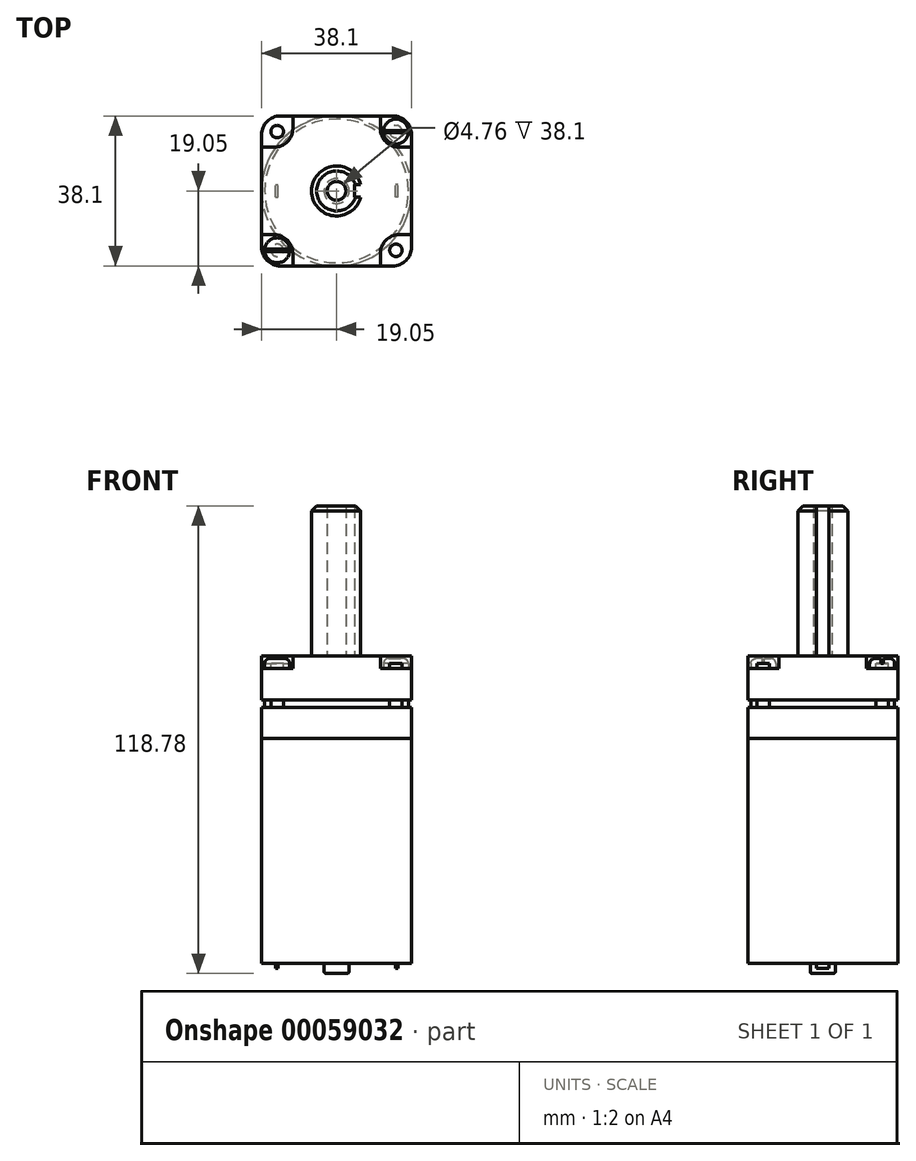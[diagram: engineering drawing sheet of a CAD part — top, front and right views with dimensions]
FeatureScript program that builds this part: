
annotation { "Feature Type Name" : "Feature", "Feature Type Description" : "" }
export const myFeature = defineFeature(function(context is Context, id is Id, definition is map)
    precondition{}
    {
        {
            var Q0;
            Q0=qCreatedBy(makeId("Top.planeOp"),FACE);
            var sketch = newSketch(context, id + "F0", { "sketchPlane" : qUnion([Q0])});
            skLineSegment(sketch, "E0.rect.bottom", {"start": v(-19.05, 19.05) * mm, "end": v(19.05, 19.05) * mm});
            skLineSegment(sketch, "E0.rect.top", {"start": v(-19.05, -19.05) * mm, "end": v(19.05, -19.05) * mm});
            skLineSegment(sketch, "E0.rect.left", {"start": v(-19.05, 19.05) * mm, "end": v(-19.05, -19.05) * mm});
            skLineSegment(sketch, "E0.rect.right", {"start": v(19.05, 19.05) * mm, "end": v(19.05, -19.05) * mm});
            skPoint(sketch, "E0.rect.middle", {"position": v(0, 0) * mm});
            skSolve(sketch);
        }
        {
            var Q0;
            Q0=qSketchRegion(id+"F0",true);
            extrude(context, id + "F1", {"entities" : qUnion([Q0]), "depth" : 7.94 * mm});
        }
        {
            var Q0;
            Q0=makeQuery(id+"F1.opExtrude","CAP_FACE",FACE,{"disambiguationData":[OSD([sQuery(id+"F0.wireOp",EDGE,"E0.rect.bottom"),sQuery(id+"F0.wireOp",EDGE,"E0.rect.top"),sQuery(id+"F0.wireOp",EDGE,"E0.rect.left"),sQuery(id+"F0.wireOp",EDGE,"E0.rect.right")])],"isStart":false});
            var sketch = newSketch(context, id + "F2", { "sketchPlane" : qUnion([Q0])});
            skCircle(sketch, "E1", {"center": v(0, 0) * mm, "radius": 18.26 * mm});
            skSolve(sketch);
        }
        {
            var Q0;
            Q0=makeQuery(id+"F2.imprint","IMPRINT",FACE,{"disambiguationData":[TD([[makeQuery(id+"F2.imprint","IMPRINT",EDGE,{"derivedFrom":sQuery(id+"F2.wireOp",EDGE,"E1")}),1.0]])]});
            extrude(context, id + "F3", {"entities" : qUnion([Q0]), "operationType" : NewBodyOperationType.ADD, "depth" : (1 + (15 / 16)) * mm});
        }
        {
            var Q0;
            Q0=makeQuery(id+"F1.opExtrude","CAP_FACE",FACE,{"disambiguationData":[OSD([sQuery(id+"F0.wireOp",EDGE,"E0.rect.bottom"),sQuery(id+"F0.wireOp",EDGE,"E0.rect.top"),sQuery(id+"F0.wireOp",EDGE,"E0.rect.left"),sQuery(id+"F0.wireOp",EDGE,"E0.rect.right")])],"isStart":true});
            var sketch = newSketch(context, id + "F4", { "sketchPlane" : qUnion([Q0])});
            skCircle(sketch, "E2", {"center": v(0, 0) * mm, "radius": 19.05 * mm});
            skSolve(sketch);
        }
        {
            var Q0;
            {var subQ0=sQuery(id+"F4.wireOp",EDGE,"E2");var subQ1=makeQuery(id+"F4.imprint","INTERSECT",VERTEX,{"derivedFrom":[makeQuery(id+"F1.opExtrude","CAP_EDGE",EDGE,{"disambiguationData":[OSD([sQuery(id+"F0.wireOp",EDGE,"E0.rect.top")])],"isStart":true}),subQ0]});Q0=makeQuery(id+"F4.imprint","IMPRINT",FACE,{"disambiguationData":[TD([[makeQuery(id+"F4.imprint","IMPRINT",EDGE,{"disambiguationData":[TD([[subQ1,1.0]])],"derivedFrom":subQ0}),1.0]])]});}
            extrude(context, id + "F5", {"entities" : qUnion([Q0]), "operationType" : NewBodyOperationType.ADD, "depth" : 57.15 * mm});
        }
        {
            var Q0;
            Q0=makeQuery(id+"F3.opExtrude","CAP_FACE",FACE,{"disambiguationData":[OSD([sQuery(id+"F2.wireOp",EDGE,"E1")])],"isStart":false});
            var sketch = newSketch(context, id + "F6", { "sketchPlane" : qUnion([Q0])});
            skLineSegment(sketch, "E3.rect.bottom", {"start": v(19.05, -19.05) * mm, "end": v(-19.05, -19.05) * mm});
            skLineSegment(sketch, "E3.rect.top", {"start": v(19.05, 19.05) * mm, "end": v(-19.05, 19.05) * mm});
            skLineSegment(sketch, "E3.rect.left", {"start": v(19.05, -19.05) * mm, "end": v(19.05, 19.05) * mm});
            skLineSegment(sketch, "E3.rect.right", {"start": v(-19.05, -19.05) * mm, "end": v(-19.05, 19.05) * mm});
            skPoint(sketch, "E3.rect.middle", {"position": v(0, 0) * mm});
            skSolve(sketch);
        }
        {
            var Q0;
            Q0=qSketchRegion(id+"F6",true);
            extrude(context, id + "F7", {"entities" : qUnion([Q0]), "operationType" : NewBodyOperationType.ADD, "depth" : 11.1 * mm});
        }
        {
            var Q0;
            Q0=makeQuery(id+"F7.opExtrude","CAP_FACE",FACE,{"disambiguationData":[OSD([sQuery(id+"F6.wireOp",EDGE,"E3.rect.bottom"),sQuery(id+"F6.wireOp",EDGE,"E3.rect.top"),sQuery(id+"F6.wireOp",EDGE,"E3.rect.left"),sQuery(id+"F6.wireOp",EDGE,"E3.rect.right")])],"isStart":false});
            var sketch = newSketch(context, id + "F8", { "sketchPlane" : qUnion([Q0])});
            skLineSegment(sketch, "E4", {"start": v(-19.05, -11.11) * mm, "end": v(-11.11, -11.11) * mm});
            skLineSegment(sketch, "E5", {"start": v(-11.11, -11.11) * mm, "end": v(-11.11, -19.05) * mm});
            skLineSegment(sketch, "E6", {"start": v(-11.11, -19.05) * mm, "end": v(-19.05, -19.05) * mm});
            skLineSegment(sketch, "E7", {"start": v(-19.05, -19.05) * mm, "end": v(-19.05, -11.11) * mm});
            skLineSegment(sketch, "E8.MirrorCS", {"start": v(11.11, -11.11) * mm, "end": v(11.11, -19.05) * mm});
            skLineSegment(sketch, "E9.MirrorCS", {"start": v(19.05, -11.11) * mm, "end": v(11.11, -11.11) * mm});
            skLineSegment(sketch, "E10.MirrorCS", {"start": v(19.05, -19.05) * mm, "end": v(19.05, -11.11) * mm});
            skLineSegment(sketch, "E11.MirrorCS", {"start": v(11.11, -19.05) * mm, "end": v(19.05, -19.05) * mm});
            skLineSegment(sketch, "E12.MirrorCS", {"start": v(19.05, 11.11) * mm, "end": v(11.11, 11.11) * mm});
            skLineSegment(sketch, "E13.MirrorCS", {"start": v(11.11, 11.11) * mm, "end": v(11.11, 19.05) * mm});
            skLineSegment(sketch, "E14.MirrorCS", {"start": v(11.11, 19.05) * mm, "end": v(19.05, 19.05) * mm});
            skLineSegment(sketch, "E15.MirrorCS", {"start": v(19.05, 19.05) * mm, "end": v(19.05, 11.11) * mm});
            skLineSegment(sketch, "E16.MirrorCS", {"start": v(-19.05, 11.11) * mm, "end": v(-11.11, 11.11) * mm});
            skLineSegment(sketch, "E17.MirrorCS", {"start": v(-11.11, 11.11) * mm, "end": v(-11.11, 19.05) * mm});
            skLineSegment(sketch, "E18.MirrorCS", {"start": v(-11.11, 19.05) * mm, "end": v(-19.05, 19.05) * mm});
            skLineSegment(sketch, "E19.MirrorCS", {"start": v(-19.05, 19.05) * mm, "end": v(-19.05, 11.11) * mm});
            skSolve(sketch);
        }
        {
            var Q0;
            Q0=makeQuery(id+"F8.imprint","IMPRINT",FACE,{"disambiguationData":[TD([[makeQuery(id+"F8.imprint","IMPRINT",EDGE,{"derivedFrom":sQuery(id+"F8.wireOp",EDGE,"E16.MirrorCS")}),1.0]])]});
            var Q1;
            Q1=makeQuery(id+"F8.imprint","IMPRINT",FACE,{"disambiguationData":[TD([[makeQuery(id+"F8.imprint","IMPRINT",EDGE,{"derivedFrom":sQuery(id+"F8.wireOp",EDGE,"E12.MirrorCS")}),-1.0]])]});
            var Q2;
            Q2=makeQuery(id+"F8.imprint","IMPRINT",FACE,{"disambiguationData":[TD([[makeQuery(id+"F8.imprint","IMPRINT",EDGE,{"derivedFrom":sQuery(id+"F8.wireOp",EDGE,"E8.MirrorCS")}),1.0]])]});
            var Q3;
            Q3=makeQuery(id+"F8.imprint","IMPRINT",FACE,{"disambiguationData":[TD([[makeQuery(id+"F8.imprint","IMPRINT",EDGE,{"derivedFrom":sQuery(id+"F8.wireOp",EDGE,"E4")}),-1.0]])]});
            extrude(context, id + "F9", {"entities" : qUnion([Q0, Q1, Q2, Q3]), "operationType" : NewBodyOperationType.REMOVE, "oppositeDirection" : true, "depth" : 3.17 * mm});
        }
        {
            var Q0;
            Q0=makeQuery(id+"F7.opExtrude","SWEPT_EDGE",EDGE,{"disambiguationData":[OSD([sQuery(id+"F6.wireOp",EDGE,"E3.rect.bottom"),sQuery(id+"F6.wireOp",EDGE,"E3.rect.right")])]});
            var Q1;
            Q1=makeQuery(id+"F7.opExtrude","SWEPT_EDGE",EDGE,{"disambiguationData":[OSD([sQuery(id+"F6.wireOp",EDGE,"E3.rect.bottom"),sQuery(id+"F6.wireOp",EDGE,"E3.rect.left")])]});
            var Q2;
            Q2=makeQuery(id+"F1.opExtrude","SWEPT_EDGE",EDGE,{"disambiguationData":[OSD([sQuery(id+"F0.wireOp",EDGE,"E0.rect.top"),sQuery(id+"F0.wireOp",EDGE,"E0.rect.right")])]});
            var Q3;
            Q3=makeQuery(id+"F1.opExtrude","SWEPT_EDGE",EDGE,{"disambiguationData":[OSD([sQuery(id+"F0.wireOp",EDGE,"E0.rect.top"),sQuery(id+"F0.wireOp",EDGE,"E0.rect.left")])]});
            var Q4;
            Q4=makeQuery(id+"F1.opExtrude","SWEPT_EDGE",EDGE,{"disambiguationData":[OSD([sQuery(id+"F0.wireOp",EDGE,"E0.rect.bottom"),sQuery(id+"F0.wireOp",EDGE,"E0.rect.right")])]});
            var Q5;
            Q5=makeQuery(id+"F7.opExtrude","SWEPT_EDGE",EDGE,{"disambiguationData":[OSD([sQuery(id+"F6.wireOp",EDGE,"E3.rect.top"),sQuery(id+"F6.wireOp",EDGE,"E3.rect.left")])]});
            var Q6;
            Q6=makeQuery(id+"F1.opExtrude","SWEPT_EDGE",EDGE,{"disambiguationData":[OSD([sQuery(id+"F0.wireOp",EDGE,"E0.rect.bottom"),sQuery(id+"F0.wireOp",EDGE,"E0.rect.left")])]});
            var Q7;
            Q7=makeQuery(id+"F7.opExtrude","SWEPT_EDGE",EDGE,{"disambiguationData":[OSD([sQuery(id+"F6.wireOp",EDGE,"E3.rect.top"),sQuery(id+"F6.wireOp",EDGE,"E3.rect.right")])]});
            fillet(context, id + "F10", {"entities" : qUnion([Q0, Q1, Q2, Q3, Q4, Q5, Q6, Q7]), "radius" : 4.76 * mm, "tangentPropagation" : true, "allowEdgeOverflow" : false});
        }
        {
            var Q0;
            Q0=makeQuery(id+"F9.boolean.opBoolean","COPY",EDGE,{"derivedFrom":makeQuery(id+"F9.opExtrude","SWEPT_EDGE",EDGE,{"disambiguationData":[OSD([sQuery(id+"F8.wireOp",EDGE,"E8.MirrorCS"),sQuery(id+"F8.wireOp",EDGE,"E9.MirrorCS")])]})});
            var Q1;
            Q1=makeQuery(id+"F9.boolean.opBoolean","COPY",EDGE,{"derivedFrom":makeQuery(id+"F9.opExtrude","SWEPT_EDGE",EDGE,{"disambiguationData":[OSD([sQuery(id+"F8.wireOp",EDGE,"E4"),sQuery(id+"F8.wireOp",EDGE,"E5")])]})});
            var Q2;
            Q2=makeQuery(id+"F9.boolean.opBoolean","COPY",EDGE,{"derivedFrom":makeQuery(id+"F9.opExtrude","SWEPT_EDGE",EDGE,{"disambiguationData":[OSD([sQuery(id+"F8.wireOp",EDGE,"E12.MirrorCS"),sQuery(id+"F8.wireOp",EDGE,"E13.MirrorCS")])]})});
            var Q3;
            Q3=makeQuery(id+"F9.boolean.opBoolean","COPY",EDGE,{"derivedFrom":makeQuery(id+"F9.opExtrude","SWEPT_EDGE",EDGE,{"disambiguationData":[OSD([sQuery(id+"F8.wireOp",EDGE,"E16.MirrorCS"),sQuery(id+"F8.wireOp",EDGE,"E17.MirrorCS")])]})});
            fillet(context, id + "F11", {"entities" : qUnion([Q0, Q1, Q2, Q3]), "radius" : 4.76 * mm, "tangentPropagation" : true, "allowEdgeOverflow" : false});
        }
        {
            var Q0;
            Q0=makeQuery(id+"F9.boolean.opBoolean","COPY",FACE,{"derivedFrom":makeQuery(id+"F9.opExtrude","CAP_FACE",FACE,{"disambiguationData":[OSD([sQuery(id+"F8.wireOp",EDGE,"E12.MirrorCS"),sQuery(id+"F8.wireOp",EDGE,"E13.MirrorCS"),sQuery(id+"F8.wireOp",EDGE,"E14.MirrorCS"),sQuery(id+"F8.wireOp",EDGE,"E15.MirrorCS")])],"isStart":false})});
            var sketch = newSketch(context, id + "F12", { "sketchPlane" : qUnion([Q0])});
            skCircle(sketch, "E20", {"center": v(15.08, 15.08) * mm, "radius": 3.18 * mm});
            skCircle(sketch, "E21.MirrorC", {"center": v(-15.08, 15.08) * mm, "radius": 3.18 * mm});
            skCircle(sketch, "E22.MirrorC", {"center": v(-15.08, -15.08) * mm, "radius": 3.18 * mm});
            skCircle(sketch, "E23.MirrorC", {"center": v(15.08, -15.08) * mm, "radius": 3.18 * mm});
            skSolve(sketch);
        }
        {
            var Q0;
            Q0=makeQuery(id+"F12.imprint","IMPRINT",FACE,{"disambiguationData":[TD([[makeQuery(id+"F12.imprint","IMPRINT",EDGE,{"derivedFrom":sQuery(id+"F12.wireOp",EDGE,"E20")}),1.0]])]});
            var Q1;
            Q1=makeQuery(id+"F12.imprint","IMPRINT",FACE,{"disambiguationData":[TD([[makeQuery(id+"F12.imprint","IMPRINT",EDGE,{"derivedFrom":sQuery(id+"F12.wireOp",EDGE,"E21.MirrorC")}),-1.0]])]});
            var Q2;
            Q2=makeQuery(id+"F12.imprint","IMPRINT",FACE,{"disambiguationData":[TD([[makeQuery(id+"F12.imprint","IMPRINT",EDGE,{"derivedFrom":sQuery(id+"F12.wireOp",EDGE,"E22.MirrorC")}),1.0]])]});
            var Q3;
            Q3=makeQuery(id+"F12.imprint","IMPRINT",FACE,{"disambiguationData":[TD([[makeQuery(id+"F12.imprint","IMPRINT",EDGE,{"derivedFrom":sQuery(id+"F12.wireOp",EDGE,"E23.MirrorC")}),-1.0]])]});
            extrude(context, id + "F13", {"entities" : qUnion([Q0, Q1, Q2, Q3]), "operationType" : NewBodyOperationType.ADD, "depth" : 2.54 * mm});
        }
        {
            var Q0;
            Q0=makeQuery(id+"F13.opExtrude","CAP_EDGE",EDGE,{"disambiguationData":[OSD([sQuery(id+"F12.wireOp",EDGE,"E21.MirrorC")])],"isStart":false});
            var Q1;
            Q1=makeQuery(id+"F13.opExtrude","CAP_EDGE",EDGE,{"disambiguationData":[OSD([sQuery(id+"F12.wireOp",EDGE,"E20")])],"isStart":false});
            var Q2;
            Q2=makeQuery(id+"F13.opExtrude","CAP_EDGE",EDGE,{"disambiguationData":[OSD([sQuery(id+"F12.wireOp",EDGE,"E23.MirrorC")])],"isStart":false});
            var Q3;
            Q3=makeQuery(id+"F13.opExtrude","CAP_EDGE",EDGE,{"disambiguationData":[OSD([sQuery(id+"F12.wireOp",EDGE,"E22.MirrorC")])],"isStart":false});
            fillet(context, id + "F14", {"entities" : qUnion([Q0, Q1, Q2, Q3]), "radius" : 1.27 * mm, "tangentPropagation" : true, "allowEdgeOverflow" : false});
        }
        {
            var Q0;
            Q0=makeQuery(id+"F13.opExtrude","CAP_FACE",FACE,{"disambiguationData":[OSD([sQuery(id+"F12.wireOp",EDGE,"E20")])],"isStart":false});
            var sketch = newSketch(context, id + "F15", { "sketchPlane" : qUnion([Q0])});
            skLineSegment(sketch, "E24.rect.bottom", {"start": v(18.39, 15.34) * mm, "end": v(11.78, 15.34) * mm});
            skLineSegment(sketch, "E24.rect.top", {"start": v(18.39, 14.82) * mm, "end": v(11.78, 14.82) * mm});
            skLineSegment(sketch, "E24.rect.left", {"start": v(18.39, 15.34) * mm, "end": v(18.39, 14.82) * mm});
            skLineSegment(sketch, "E24.rect.right", {"start": v(11.78, 15.34) * mm, "end": v(11.78, 14.82) * mm});
            skPoint(sketch, "E24.rect.middle", {"position": v(15.08, 15.08) * mm});
            skLineSegment(sketch, "E25.MirrorCS", {"start": v(-18.39, 15.34) * mm, "end": v(-11.78, 15.34) * mm});
            skLineSegment(sketch, "E26.MirrorCS", {"start": v(-18.39, 14.82) * mm, "end": v(-11.78, 14.82) * mm});
            skLineSegment(sketch, "E27.MirrorCS", {"start": v(-11.78, 15.34) * mm, "end": v(-11.78, 14.82) * mm});
            skLineSegment(sketch, "E28.MirrorCS", {"start": v(-18.39, 15.34) * mm, "end": v(-18.39, 14.82) * mm});
            skLineSegment(sketch, "E29.MirrorCS", {"start": v(18.39, -15.34) * mm, "end": v(11.78, -15.34) * mm});
            skLineSegment(sketch, "E30.MirrorCS", {"start": v(18.39, -14.82) * mm, "end": v(11.78, -14.82) * mm});
            skLineSegment(sketch, "E31.MirrorCS", {"start": v(11.78, -15.34) * mm, "end": v(11.78, -14.82) * mm});
            skLineSegment(sketch, "E32.MirrorCS", {"start": v(18.39, -15.34) * mm, "end": v(18.39, -14.82) * mm});
            skLineSegment(sketch, "E33.MirrorCS", {"start": v(-18.39, -14.82) * mm, "end": v(-11.78, -14.82) * mm});
            skLineSegment(sketch, "E34.MirrorCS", {"start": v(-18.39, -15.34) * mm, "end": v(-11.78, -15.34) * mm});
            skLineSegment(sketch, "E35.MirrorCS", {"start": v(-11.78, -15.34) * mm, "end": v(-11.78, -14.82) * mm});
            skLineSegment(sketch, "E36.MirrorCS", {"start": v(-18.39, -15.34) * mm, "end": v(-18.39, -14.82) * mm});
            skSolve(sketch);
        }
        {
            var Q0;
            Q0=qSketchRegion(id+"F15",true);
            extrude(context, id + "F16", {"entities" : qUnion([Q0]), "operationType" : NewBodyOperationType.REMOVE, "oppositeDirection" : true, "depth" : 1.27 * mm});
        }
        {
            var Q0;
            Q0=makeQuery(id+"F16.boolean.opBoolean","COPY",FACE,{"derivedFrom":makeQuery(id+"F16.opExtrude","CAP_FACE",FACE,{"disambiguationData":[OSD([sQuery(id+"F15.wireOp",EDGE,"E24.rect.bottom"),sQuery(id+"F15.wireOp",EDGE,"E24.rect.top"),sQuery(id+"F15.wireOp",EDGE,"E24.rect.left"),sQuery(id+"F15.wireOp",EDGE,"E24.rect.right")])],"isStart":false})});
            var sketch = newSketch(context, id + "F17", { "sketchPlane" : qUnion([Q0])});
            skCircle(sketch, "E37", {"center": v(15.08, 15.08) * mm, "radius": 1.59 * mm});
            skCircle(sketch, "E38.MirrorC", {"center": v(-15.08, 15.08) * mm, "radius": 1.59 * mm});
            skCircle(sketch, "E39.MirrorC", {"center": v(-15.08, -15.08) * mm, "radius": 1.59 * mm});
            skCircle(sketch, "E40.MirrorC", {"center": v(15.08, -15.08) * mm, "radius": 1.59 * mm});
            skSolve(sketch);
        }
        {
            var Q0;
            Q0=qSketchRegion(id+"F17",true);
            var Q1;
            Q1=makeQuery(id+"F1.opExtrude","CAP_FACE",FACE,{"disambiguationData":[OSD([sQuery(id+"F0.wireOp",EDGE,"E0.rect.bottom"),sQuery(id+"F0.wireOp",EDGE,"E0.rect.top"),sQuery(id+"F0.wireOp",EDGE,"E0.rect.left"),sQuery(id+"F0.wireOp",EDGE,"E0.rect.right")])],"isStart":false});
            extrude(context, id + "F18", {"entities" : qUnion([Q0]), "operationType" : NewBodyOperationType.ADD, "endBound" : BoundingType.UP_TO_SURFACE, "oppositeDirection" : true, "endBoundEntityFace" : qUnion([Q1]), "depth" : 25.4 * mm});
        }
        {
            var Q0;
            Q0=makeQuery(id+"F5.opExtrude","CAP_FACE",FACE,{"disambiguationData":[OSD([sQuery(id+"F4.wireOp",EDGE,"E2")])],"isStart":false});
            var sketch = newSketch(context, id + "F19", { "sketchPlane" : qUnion([Q0])});
            skCircle(sketch, "E41", {"center": v(0, 0) * mm, "radius": 3.18 * mm});
            skLineSegment(sketch, "E42.rect.bottom", {"start": v(15.56, 1.59) * mm, "end": v(14.92, 1.59) * mm});
            skLineSegment(sketch, "E42.rect.top", {"start": v(15.56, -1.59) * mm, "end": v(14.92, -1.59) * mm});
            skLineSegment(sketch, "E42.rect.left", {"start": v(15.56, 1.59) * mm, "end": v(15.56, -1.59) * mm});
            skLineSegment(sketch, "E42.rect.right", {"start": v(14.92, 1.59) * mm, "end": v(14.92, -1.59) * mm});
            skPoint(sketch, "E42.rect.middle", {"position": v(15.24, 0) * mm});
            skLineSegment(sketch, "E43.MirrorCS", {"start": v(-15.56, -1.59) * mm, "end": v(-14.92, -1.59) * mm});
            skLineSegment(sketch, "E44.MirrorCS", {"start": v(-15.56, 1.59) * mm, "end": v(-14.92, 1.59) * mm});
            skPoint(sketch, "E45.MirrorP", {"position": v(-15.24, 0) * mm});
            skLineSegment(sketch, "E46.MirrorCS", {"start": v(-14.92, 1.59) * mm, "end": v(-14.92, -1.59) * mm});
            skLineSegment(sketch, "E47.MirrorCS", {"start": v(-15.56, 1.59) * mm, "end": v(-15.56, -1.59) * mm});
            skSolve(sketch);
        }
        {
            var Q0;
            Q0=makeQuery(id+"F19.imprint","IMPRINT",FACE,{"disambiguationData":[TD([[makeQuery(id+"F19.imprint","IMPRINT",EDGE,{"derivedFrom":sQuery(id+"F19.wireOp",EDGE,"E41")}),1.0]])]});
            extrude(context, id + "F20", {"entities" : qUnion([Q0]), "operationType" : NewBodyOperationType.ADD, "depth" : 2.54 * mm});
        }
        {
            var Q0;
            Q0=makeQuery(id+"F7.opExtrude","CAP_FACE",FACE,{"disambiguationData":[OSD([sQuery(id+"F6.wireOp",EDGE,"E3.rect.bottom"),sQuery(id+"F6.wireOp",EDGE,"E3.rect.top"),sQuery(id+"F6.wireOp",EDGE,"E3.rect.left"),sQuery(id+"F6.wireOp",EDGE,"E3.rect.right")])],"isStart":false});
            var sketch = newSketch(context, id + "F21", { "sketchPlane" : qUnion([Q0])});
            skCircle(sketch, "E48", {"center": v(0, 0) * mm, "radius": 2.38 * mm});
            skLineSegment(sketch, "E49", {"start": v(4.56, 0) * mm, "end": v(4.56, -1.59) * mm});
            skLineSegment(sketch, "E50", {"start": v(4.56, -1.59) * mm, "end": v(6.15, -1.59) * mm});
            skLineSegment(sketch, "E51", {"start": v(4.56, 0) * mm, "end": v(4.56, 1.59) * mm});
            skLineSegment(sketch, "E52", {"start": v(4.56, 1.59) * mm, "end": v(6.15, 1.59) * mm});
            skArc(sketch, "E53", {"start": v(6.15, 1.59) * mm, "mid": v(-6.35, 0) * mm, "end": v(6.15, -1.59) * mm});
            skSolve(sketch);
        }
        {
            var Q0;
            Q0=qSketchRegion(id+"F19",true);
            extrude(context, id + "F22", {"entities" : qUnion([Q0]), "operationType" : NewBodyOperationType.ADD, "depth" : 1.27 * mm});
        }
        {
            var Q0;
            Q0=makeQuery(id+"F20.opExtrude","SWEPT_FACE",FACE,{"disambiguationData":[OSD([sQuery(id+"F19.wireOp",EDGE,"E41")])]});
            fillet(context, id + "F23", {"entities" : qUnion([Q0]), "radius" : 0.5 * mm, "tangentPropagation" : true, "allowEdgeOverflow" : false});
        }
        {
            var Q0;
            Q0=qSketchRegion(id+"F21",true);
            extrude(context, id + "F24", {"entities" : qUnion([Q0]), "operationType" : NewBodyOperationType.ADD, "depth" : 38.1 * mm});
        }
        {
            var Q0;
            Q0=makeQuery(id+"F24.opExtrude","CAP_EDGE",EDGE,{"disambiguationData":[OSD([sQuery(id+"F21.wireOp",EDGE,"E53")])],"isStart":false});
            chamfer(context, id + "F25", {"entities" : qUnion([Q0]), "width" : 1.27 * mm, "tangentPropagation" : true});
        }
    });
